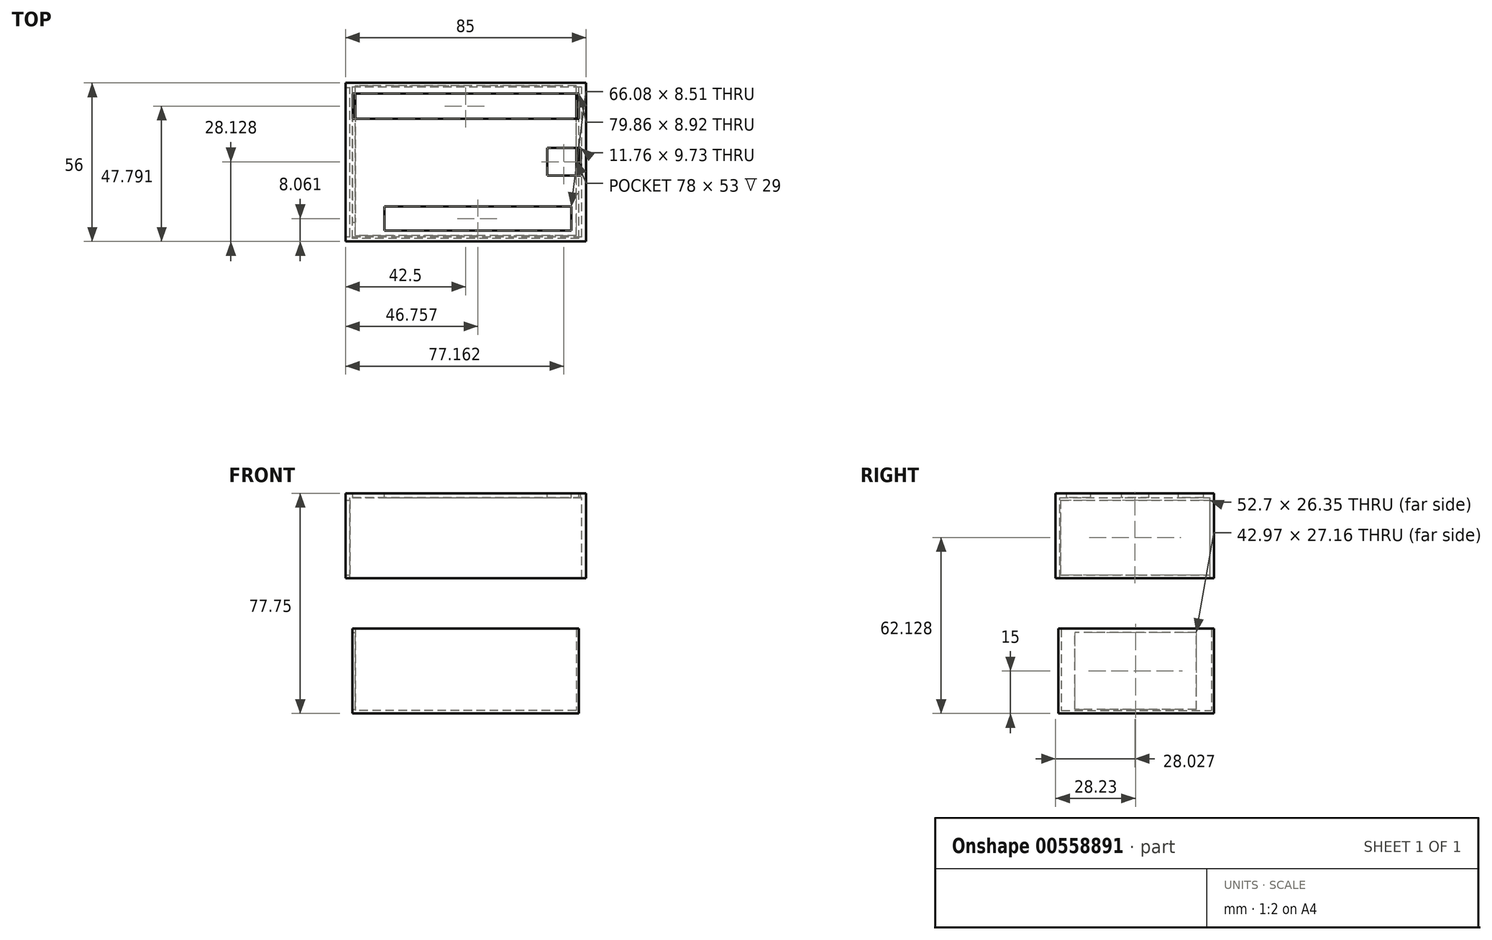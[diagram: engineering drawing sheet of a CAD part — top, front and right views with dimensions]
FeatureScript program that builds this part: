
annotation { "Feature Type Name" : "Feature", "Feature Type Description" : "" }
export const myFeature = defineFeature(function(context is Context, id is Id, definition is map)
    precondition{}
    {
        {
            var Q0;
            Q0=qCreatedBy(makeId("Front.planeOp"),FACE);
            var sketch = newSketch(context, id + "F0", { "sketchPlane" : qUnion([Q0])});
            skLineSegment(sketch, "E0.bottom", {"start": v(40, 15) * mm, "end": v(-40, 15) * mm});
            skLineSegment(sketch, "E0.top", {"start": v(40, -15) * mm, "end": v(-40, -15) * mm});
            skLineSegment(sketch, "E0.left", {"start": v(40, 15) * mm, "end": v(40, -15) * mm});
            skLineSegment(sketch, "E0.right", {"start": v(-40, 15) * mm, "end": v(-40, -15) * mm});
            skPoint(sketch, "E0.middle", {"position": v(0, 0) * mm});
            skSolve(sketch);
        }
        {
            var Q0;
            Q0=makeQuery(id+"F0.imprint","IMPRINT",FACE,{"disambiguationData":[TD([[makeQuery(id+"F0.imprint","IMPRINT",EDGE,{"derivedFrom":sQuery(id+"F0.wireOp",EDGE,"E0.bottom")}),1.0]])]});
            extrude(context, id + "F1", {"entities" : qUnion([Q0]), "depth" : 55 * mm, "offsetDistance" : 25 * mm});
        }
        {
            var Q0;
            Q0=makeQuery(id+"F1.opExtrude","SWEPT_FACE",FACE,{"disambiguationData":[OSD([sQuery(id+"F0.wireOp",EDGE,"E0.bottom")])]});
            shell(context, id + "F2", {"entities" : qUnion([Q0]), "thickness" : 1 * mm});
        }
        {
            var Q0;
            Q0=qCreatedBy(makeId("Front.planeOp"),FACE);
            var sketch = newSketch(context, id + "F3", { "sketchPlane" : qUnion([Q0])});
            skLineSegment(sketch, "E1.bottom", {"start": v(42.5, 32.75) * mm, "end": v(-42.5, 32.75) * mm});
            skLineSegment(sketch, "E1.top", {"start": v(42.5, 62.75) * mm, "end": v(-42.5, 62.75) * mm});
            skLineSegment(sketch, "E1.left", {"start": v(42.5, 32.75) * mm, "end": v(42.5, 62.75) * mm});
            skLineSegment(sketch, "E1.right", {"start": v(-42.5, 32.75) * mm, "end": v(-42.5, 62.75) * mm});
            skPoint(sketch, "E1.middle", {"position": v(0, 47.75) * mm});
            skSolve(sketch);
        }
        {
            var Q0;
            Q0=makeQuery(id+"F3.imprint","IMPRINT",FACE,{"disambiguationData":[TD([[makeQuery(id+"F3.imprint","IMPRINT",EDGE,{"derivedFrom":sQuery(id+"F3.wireOp",EDGE,"E1.bottom")}),-1.0]])]});
            extrude(context, id + "F4", {"entities" : qUnion([Q0]), "depth" : 56 * mm, "offsetDistance" : 25 * mm});
        }
        {
            var Q0;
            Q0=makeQuery(id+"F4.opExtrude","SWEPT_FACE",FACE,{"disambiguationData":[OSD([sQuery(id+"F3.wireOp",EDGE,"E1.bottom")])]});
            shell(context, id + "F5", {"entities" : qUnion([Q0]), "thickness" : 1.5 * mm});
        }
        {
            var Q0;
            Q0=qCreatedBy(makeId("Right.planeOp"),FACE);
            var sketch = newSketch(context, id + "F6", { "sketchPlane" : qUnion([Q0])});
            skLineSegment(sketch, "E2.bottom", {"start": v(-1.62, 33.95) * mm, "end": v(-54.32, 33.95) * mm});
            skLineSegment(sketch, "E2.top", {"start": v(-1.62, 60.3) * mm, "end": v(-54.32, 60.3) * mm});
            skLineSegment(sketch, "E2.left", {"start": v(-1.62, 33.95) * mm, "end": v(-1.62, 60.3) * mm});
            skLineSegment(sketch, "E2.right", {"start": v(-54.32, 33.95) * mm, "end": v(-54.32, 60.3) * mm});
            skPoint(sketch, "E2.middle", {"position": v(-27.97, 47.13) * mm});
            skSolve(sketch);
        }
        {
            var Q0;
            Q0 = qSketchRegion(id + "F6", true);
            extrude(context, id + "F7", {"entities" : qUnion([Q0]), "operationType" : NewBodyOperationType.REMOVE, "oppositeDirection" : true, "depth" : 50 * mm, "offsetDistance" : 25 * mm});
        }
        {
            var Q0;
            Q0=qCreatedBy(makeId("Right.planeOp"),FACE);
            var sketch = newSketch(context, id + "F8", { "sketchPlane" : qUnion([Q0])});
            skLineSegment(sketch, "E3.bottom", {"start": v(-6.28, -13.58) * mm, "end": v(-49.26, -13.58) * mm});
            skLineSegment(sketch, "E3.top", {"start": v(-6.28, 13.58) * mm, "end": v(-49.26, 13.58) * mm});
            skLineSegment(sketch, "E3.left", {"start": v(-6.28, -13.58) * mm, "end": v(-6.28, 13.58) * mm});
            skLineSegment(sketch, "E3.right", {"start": v(-49.26, -13.58) * mm, "end": v(-49.26, 13.58) * mm});
            skPoint(sketch, "E3.middle", {"position": v(-27.77, 0) * mm});
            skSolve(sketch);
        }
        {
            var Q0;
            Q0 = qSketchRegion(id + "F8", true);
            extrude(context, id + "F9", {"entities" : qUnion([Q0]), "operationType" : NewBodyOperationType.REMOVE, "oppositeDirection" : true, "depth" : 50 * mm, "offsetDistance" : 25 * mm});
        }
        {
            var Q0;
            Q0=makeQuery(id+"F4.opExtrude","SWEPT_FACE",FACE,{"disambiguationData":[OSD([sQuery(id+"F3.wireOp",EDGE,"E1.top")])]});
            var sketch = newSketch(context, id + "F10", { "sketchPlane" : qUnion([Q0])});
            skLineSegment(sketch, "E4.bottom", {"start": v(39.93, -12.67) * mm, "end": v(-39.93, -12.67) * mm});
            skLineSegment(sketch, "E4.top", {"start": v(39.93, -3.75) * mm, "end": v(-39.93, -3.75) * mm});
            skLineSegment(sketch, "E4.left", {"start": v(39.93, -12.67) * mm, "end": v(39.93, -3.75) * mm});
            skLineSegment(sketch, "E4.right", {"start": v(-39.93, -12.67) * mm, "end": v(-39.93, -3.75) * mm});
            skPoint(sketch, "E4.middle", {"position": v(0, -8.2) * mm});
            skSolve(sketch);
        }
        {
            var Q0;
            Q0 = qSketchRegion(id + "F10", true);
            extrude(context, id + "F11", {"entities" : qUnion([Q0]), "operationType" : NewBodyOperationType.REMOVE, "oppositeDirection" : true, "depth" : 25 * mm, "offsetDistance" : 25 * mm});
        }
        {
            var Q0;
            Q0=makeQuery(id+"F4.opExtrude","SWEPT_FACE",FACE,{"disambiguationData":[OSD([sQuery(id+"F3.wireOp",EDGE,"E1.top")])]});
            var sketch = newSketch(context, id + "F12", { "sketchPlane" : qUnion([Q0])});
            skLineSegment(sketch, "E5.bottom", {"start": v(37.3, -52.2) * mm, "end": v(-28.78, -52.2) * mm});
            skLineSegment(sketch, "E5.top", {"start": v(37.3, -43.68) * mm, "end": v(-28.78, -43.68) * mm});
            skLineSegment(sketch, "E5.left", {"start": v(37.3, -52.2) * mm, "end": v(37.3, -43.68) * mm});
            skLineSegment(sketch, "E5.right", {"start": v(-28.78, -52.2) * mm, "end": v(-28.78, -43.68) * mm});
            skPoint(sketch, "E5.middle", {"position": v(4.26, -47.94) * mm});
            skSolve(sketch);
        }
        {
            var Q0;
            Q0 = qSketchRegion(id + "F12", true);
            extrude(context, id + "F13", {"entities" : qUnion([Q0]), "operationType" : NewBodyOperationType.REMOVE, "oppositeDirection" : true, "depth" : 25 * mm, "offsetDistance" : 25 * mm});
        }
        {
            var Q0;
            Q0=makeQuery(id+"F4.opExtrude","SWEPT_FACE",FACE,{"disambiguationData":[OSD([sQuery(id+"F3.wireOp",EDGE,"E1.top")])]});
            var sketch = newSketch(context, id + "F14", { "sketchPlane" : qUnion([Q0])});
            skLineSegment(sketch, "E6.bottom", {"start": v(40.54, -32.74) * mm, "end": v(28.78, -32.74) * mm});
            skLineSegment(sketch, "E6.top", {"start": v(40.54, -23) * mm, "end": v(28.78, -23) * mm});
            skLineSegment(sketch, "E6.left", {"start": v(40.54, -32.74) * mm, "end": v(40.54, -23) * mm});
            skLineSegment(sketch, "E6.right", {"start": v(28.78, -32.74) * mm, "end": v(28.78, -23) * mm});
            skPoint(sketch, "E6.middle", {"position": v(34.66, -27.87) * mm});
            skSolve(sketch);
        }
        {
            var Q0;
            Q0 = qSketchRegion(id + "F14", true);
            extrude(context, id + "F15", {"entities" : qUnion([Q0]), "operationType" : NewBodyOperationType.REMOVE, "oppositeDirection" : true, "depth" : 25 * mm, "offsetDistance" : 25 * mm});
        }
    });
